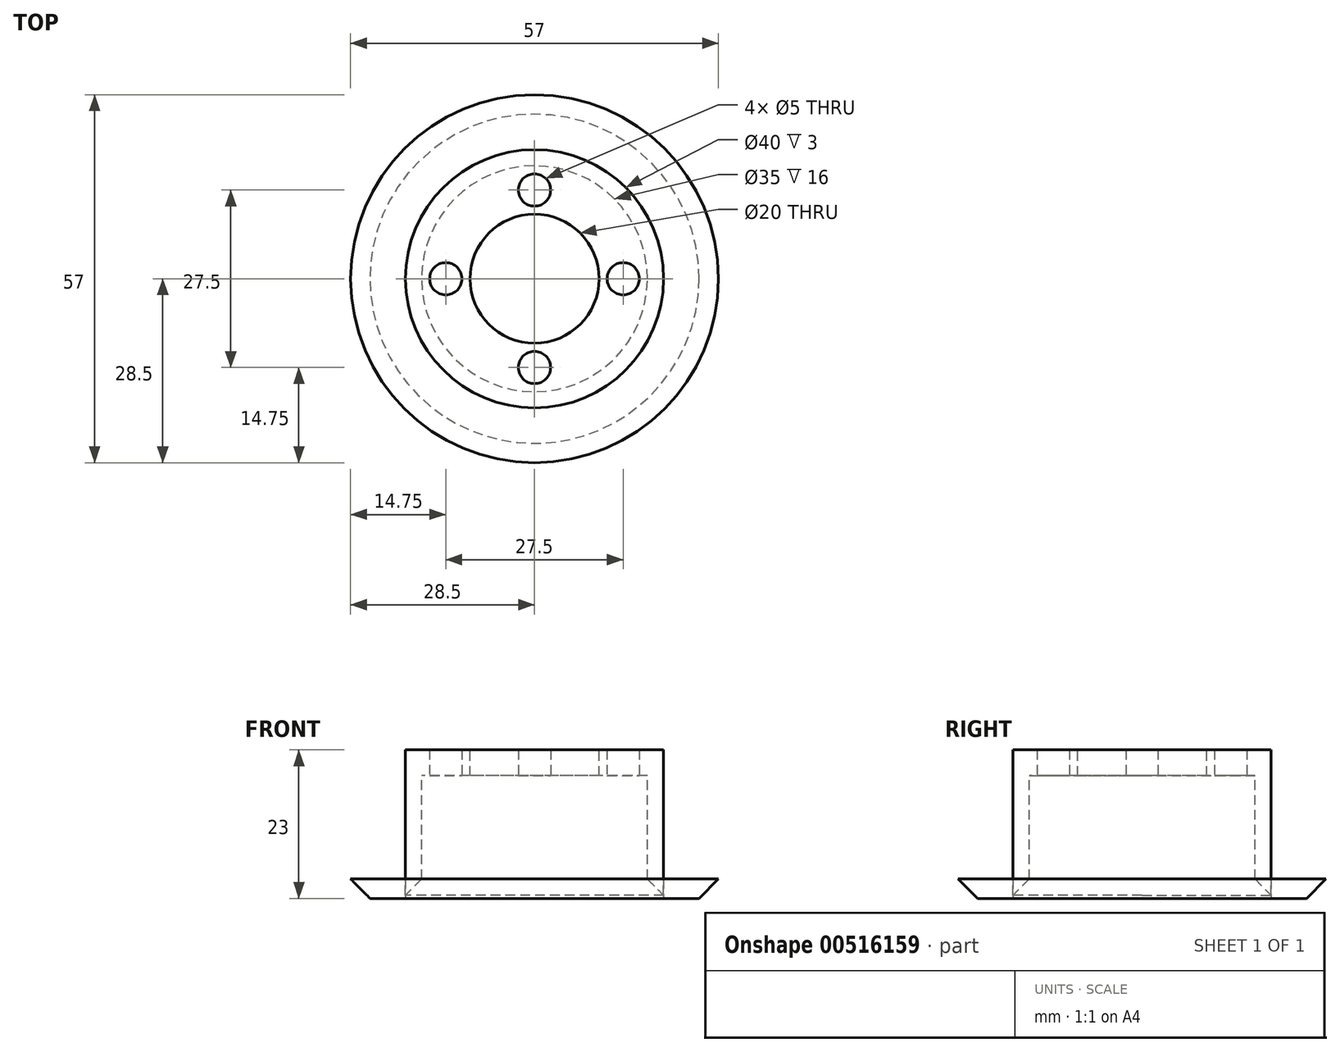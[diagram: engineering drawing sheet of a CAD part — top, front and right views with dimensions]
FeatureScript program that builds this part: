
annotation { "Feature Type Name" : "Feature", "Feature Type Description" : "" }
export const myFeature = defineFeature(function(context is Context, id is Id, definition is map)
    precondition{}
    {
        {
            var Q0;
            Q0=qCreatedBy(makeId("Top.planeOp"),FACE);
            var sketch = newSketch(context, id + "F0", { "sketchPlane" : qUnion([Q0])});
            skCircle(sketch, "E0", {"center": v(0, 0) * mm, "radius": 20 * mm});
            skCircle(sketch, "E1", {"center": v(0, 0) * mm, "radius": 10 * mm});
            skCircle(sketch, "E2", {"center": v(0, 0) * mm, "radius": 17.5 * mm});
            skSolve(sketch);
        }
        {
            var Q0;
            Q0=makeQuery(id+"F0.imprint","IMPRINT",FACE,{"disambiguationData":[TD([[makeQuery(id+"F0.imprint","IMPRINT",EDGE,{"derivedFrom":sQuery(id+"F0.wireOp",EDGE,"E0")}),1.0]])]});
            extrude(context, id + "F1", {"entities" : qUnion([Q0]), "oppositeDirection" : true, "depth" : 23 * mm, "offsetDistance" : 25 * mm});
        }
        {
            var Q0;
            Q0=makeQuery(id+"F0.imprint","IMPRINT",FACE,{"disambiguationData":[TD([[makeQuery(id+"F0.imprint","IMPRINT",EDGE,{"derivedFrom":sQuery(id+"F0.wireOp",EDGE,"E1")}),-1.0]])]});
            extrude(context, id + "F2", {"entities" : qUnion([Q0]), "operationType" : NewBodyOperationType.ADD, "oppositeDirection" : true, "depth" : 4 * mm, "offsetDistance" : 25 * mm});
        }
        {
            var Q0;
            Q0=makeQuery(id+"F1.opExtrude","CAP_FACE",FACE,{"disambiguationData":[OSD([sQuery(id+"F0.wireOp",EDGE,"E0"),sQuery(id+"F0.wireOp",EDGE,"E2")])],"isStart":false});
            var sketch = newSketch(context, id + "F3", { "sketchPlane" : qUnion([Q0])});
            skCircle(sketch, "E3", {"center": v(0, 0) * mm, "radius": 28.5 * mm});
            skSolve(sketch);
        }
        {
            var Q0;
            Q0=makeQuery(id+"F3.imprint","IMPRINT",FACE,{"disambiguationData":[TD([[makeQuery(id+"F3.imprint","IMPRINT",EDGE,{"derivedFrom":sQuery(id+"F3.wireOp",EDGE,"E3")}),1.0]])]});
            extrude(context, id + "F4", {"entities" : qUnion([Q0]), "oppositeDirection" : true, "depth" : 3 * mm, "offsetDistance" : 25 * mm});
        }
        {
            var Q0;
            Q0=makeQuery(id+"F2.opExtrude","CAP_FACE",FACE,{"disambiguationData":[OSD([sQuery(id+"F0.wireOp",EDGE,"E1"),sQuery(id+"F0.wireOp",EDGE,"E2")])],"isStart":false});
            var sketch = newSketch(context, id + "F5", { "sketchPlane" : qUnion([Q0])});
            skCircle(sketch, "E4", {"center": v(0, 13.75) * mm, "radius": 2.5 * mm});
            skCircle(sketch, "E5.1.0", {"center": v(-13.75, 0) * mm, "radius": 2.5 * mm});
            skCircle(sketch, "E5.2.0", {"center": v(0, -13.75) * mm, "radius": 2.5 * mm});
            skCircle(sketch, "E5.3.0", {"center": v(13.75, 0) * mm, "radius": 2.5 * mm});
            skPoint(sketch, "E5.center", {"position": v(0, 0) * mm});
            skSolve(sketch);
        }
        {
            var Q0;
            Q0 = qSketchRegion(id + "F5", true);
            extrude(context, id + "F6", {"entities" : qUnion([Q0]), "operationType" : NewBodyOperationType.REMOVE, "endBound" : BoundingType.THROUGH_ALL, "oppositeDirection" : true, "depth" : 25 * mm, "offsetDistance" : 25 * mm});
        }
        {
            var Q0;
            Q0=makeQuery(id+"F4.opExtrude","CAP_EDGE",EDGE,{"disambiguationData":[OSD([sQuery(id+"F3.wireOp",EDGE,"E3")])],"isStart":true});
            chamfer(context, id + "F7", {"entities" : qUnion([Q0]), "width" : 3 * mm, "tangentPropagation" : true});
        }
        {
            var Q0;
            Q0=makeQuery(id+"F1.opExtrude","CAP_EDGE",EDGE,{"disambiguationData":[OSD([sQuery(id+"F0.wireOp",EDGE,"E2")])],"isStart":false});
            chamfer(context, id + "F8", {"entities" : qUnion([Q0]), "width" : 3 * mm, "tangentPropagation" : true});
        }
    });
